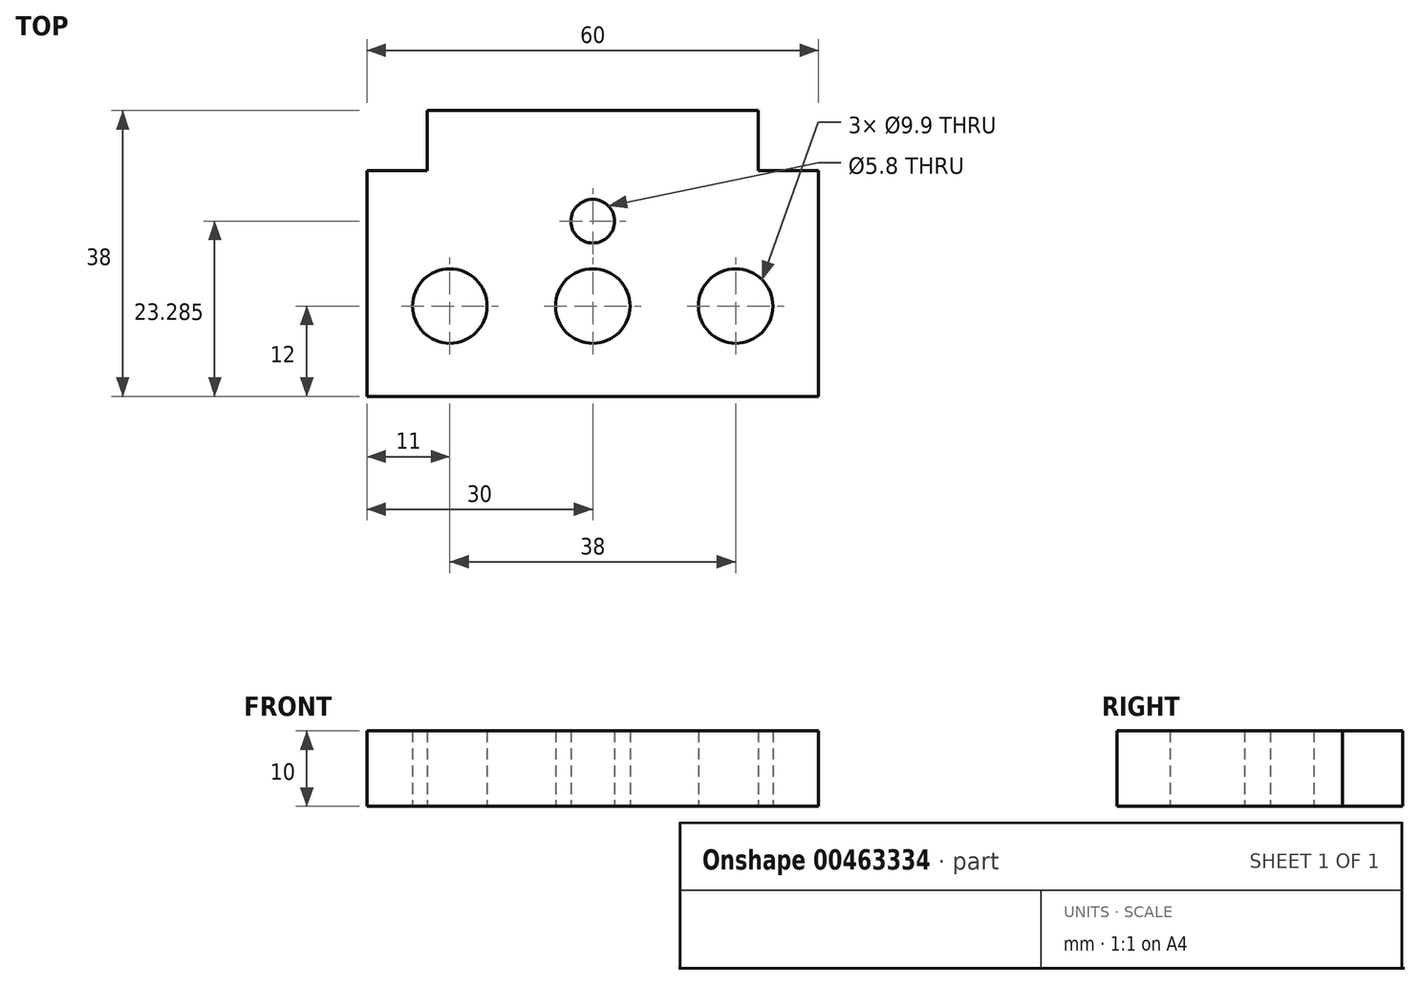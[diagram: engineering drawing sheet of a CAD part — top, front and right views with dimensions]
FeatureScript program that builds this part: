
annotation { "Feature Type Name" : "Feature", "Feature Type Description" : "" }
export const myFeature = defineFeature(function(context is Context, id is Id, definition is map)
    precondition{}
    {
        {
            var Q0;
            Q0=qCreatedBy(makeId("Top.planeOp"),FACE);
            var sketch = newSketch(context, id + "F0", { "sketchPlane" : qUnion([Q0])});
            skLineSegment(sketch, "E0.bottom", {"start": v(30, -15) * mm, "end": v(-30, -15) * mm});
            skLineSegment(sketch, "E0.top", {"start": v(30, 15) * mm, "end": v(-30, 15) * mm});
            skLineSegment(sketch, "E0.left", {"start": v(30, -15) * mm, "end": v(30, 15) * mm});
            skLineSegment(sketch, "E0.right", {"start": v(-30, -15) * mm, "end": v(-30, 15) * mm});
            skPoint(sketch, "E0.middle", {"position": v(0, 0) * mm});
            skCircle(sketch, "E1", {"center": v(0, 8.28) * mm, "radius": 2.9 * mm});
            skLineSegment(sketch, "E2", {"start": v(-30, -3) * mm, "end": v(30, -3) * mm});
            skCircle(sketch, "E3", {"center": v(0, -3) * mm, "radius": 4.95 * mm});
            skCircle(sketch, "E4", {"center": v(-19, -3) * mm, "radius": 4.95 * mm});
            skCircle(sketch, "E5", {"center": v(19, -3) * mm, "radius": 4.95 * mm});
            skLineSegment(sketch, "E6", {"start": v(-22, 15) * mm, "end": v(-22, 23) * mm});
            skLineSegment(sketch, "E7", {"start": v(-22, 23) * mm, "end": v(22, 23) * mm});
            skLineSegment(sketch, "E8", {"start": v(22, 23) * mm, "end": v(22, 15) * mm});
            skLineSegment(sketch, "E9", {"start": v(22, 15) * mm, "end": v(-22, 15) * mm});
            skSolve(sketch);
        }
        {
            var Q0;
            Q0=makeQuery(id+"F0.imprint","IMPRINT",FACE,{"disambiguationData":[TD([[makeQuery(id+"F0.imprint","IMPRINT",EDGE,{"derivedFrom":sQuery(id+"F0.wireOp",EDGE,"E1")}),-1.0]])]});
            var Q1;
            {var subQ6=sQuery(id+"F0.wireOp",EDGE,"E0.bottom");Q1=makeQuery(id+"F0.imprint","IMPRINT",FACE,{"disambiguationData":[TD([[makeQuery(id+"F0.imprint","IMPRINT",EDGE,{"derivedFrom":subQ6}),-1.0]])]});}
            var Q2;
            Q2=makeQuery(id+"F0.imprint","IMPRINT",FACE,{"disambiguationData":[TD([[makeQuery(id+"F0.imprint","IMPRINT",EDGE,{"derivedFrom":sQuery(id+"F0.wireOp",EDGE,"E6")}),-1.0]])]});
            extrude(context, id + "F1", {"entities" : qUnion([Q0, Q1, Q2]), "depth" : 10 * mm});
        }
    });
